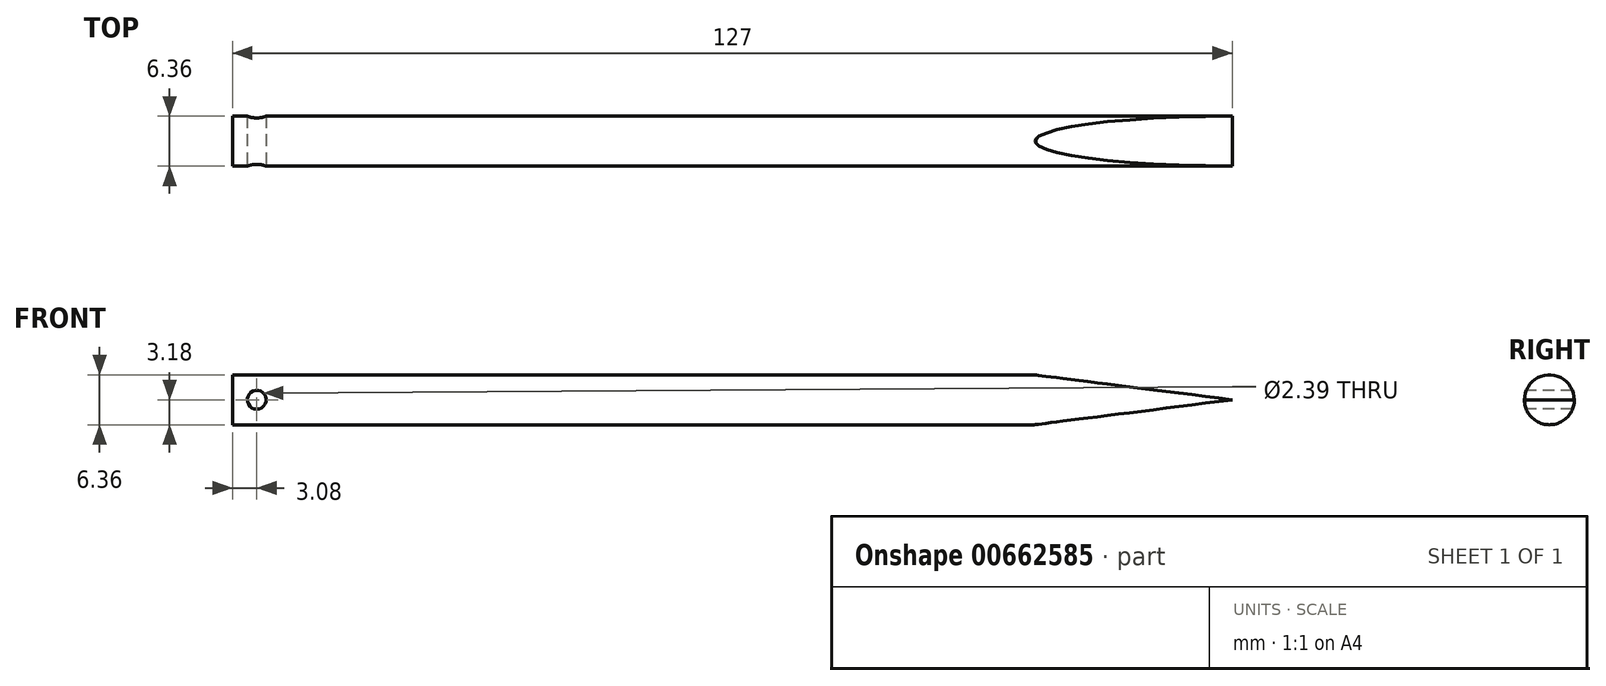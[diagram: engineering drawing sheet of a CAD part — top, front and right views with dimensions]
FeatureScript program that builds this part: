
annotation { "Feature Type Name" : "Feature", "Feature Type Description" : "" }
export const myFeature = defineFeature(function(context is Context, id is Id, definition is map)
    precondition{}
    {
        {
            var Q0;
            Q0=qCreatedBy(makeId("Right.planeOp"),FACE);
            var sketch = newSketch(context, id + "F0", { "sketchPlane" : qUnion([Q0])});
            skCircle(sketch, "E0", {"center": v(0, 0) * mm, "radius": 3.18 * mm});
            skSolve(sketch);
        }
        {
            var Q0;
            Q0=qSketchRegion(id+"F0",true);
            extrude(context, id + "F1", {"entities" : qUnion([Q0]), "oppositeDirection" : true, "depth" : 127 * mm, "offsetDistance" : 25.4 * mm});
        }
        {
            var Q0;
            Q0=qCreatedBy(makeId("Front.planeOp"),FACE);
            var sketch = newSketch(context, id + "F2", { "sketchPlane" : qUnion([Q0])});
            skLineSegment(sketch, "E1", {"start": v(-25.2, 3.18) * mm, "end": v(0, 0) * mm});
            skLineSegment(sketch, "E2", {"start": v(-25.2, 3.18) * mm, "end": v(-25.2, 5.16) * mm});
            skLineSegment(sketch, "E3", {"start": v(-25.2, 5.16) * mm, "end": v(0, 5.16) * mm});
            skLineSegment(sketch, "E4", {"start": v(0, 5.16) * mm, "end": v(0, 0) * mm});
            skLineSegment(sketch, "E5", {"start": v(-25.2, 0) * mm, "end": v(0, 0) * mm});
            skPoint(sketch, "E5.startSnap0", {"position": v(-25.2, 4.17) * mm});
            skLineSegment(sketch, "E6.MirrorCS", {"start": v(-25.2, -3.18) * mm, "end": v(-25.2, -5.16) * mm});
            skLineSegment(sketch, "E7.MirrorCS", {"start": v(-25.2, -5.16) * mm, "end": v(0, -5.16) * mm});
            skPoint(sketch, "E8.MirrorP", {"position": v(-25.2, -4.17) * mm});
            skLineSegment(sketch, "E9.MirrorCS", {"start": v(0, -5.16) * mm, "end": v(0, 0) * mm});
            skLineSegment(sketch, "E10.MirrorCS", {"start": v(-25.2, -3.18) * mm, "end": v(0, 0) * mm});
            skCircle(sketch, "E11", {"center": v(-123.92, 0) * mm, "radius": 1.2 * mm});
            skSolve(sketch);
        }
        {
            var Q0;
            Q0=qSketchRegion(id+"F2",true);
            extrude(context, id + "F3", {"entities" : qUnion([Q0]), "operationType" : NewBodyOperationType.REMOVE, "endBound" : BoundingType.SYMMETRIC, "oppositeDirection" : true, "depth" : 25.4 * mm, "offsetDistance" : 25.4 * mm});
        }
    });
